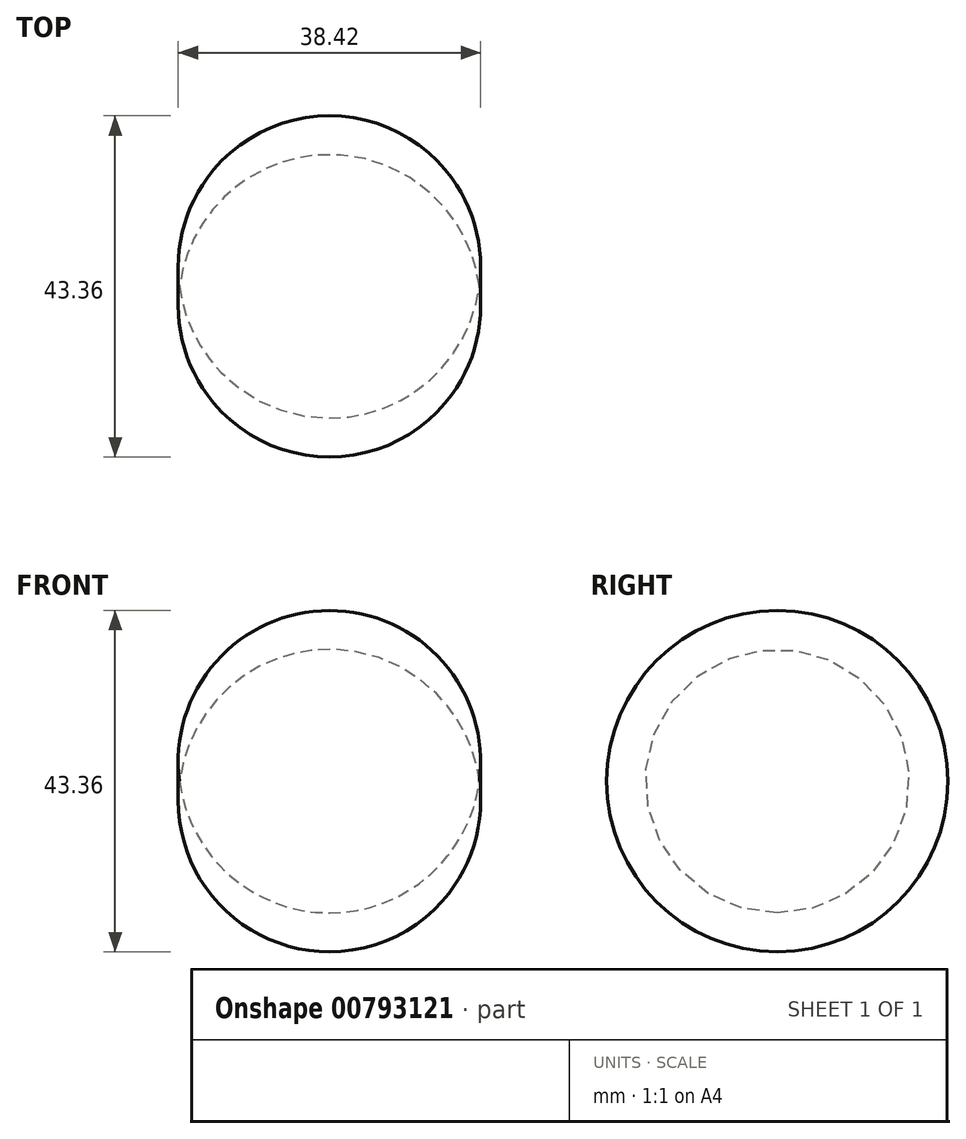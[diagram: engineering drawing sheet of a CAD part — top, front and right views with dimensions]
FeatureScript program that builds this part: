
annotation { "Feature Type Name" : "Feature", "Feature Type Description" : "" }
export const myFeature = defineFeature(function(context is Context, id is Id, definition is map)
    precondition{}
    {
        {
            var Q0;
            Q0=qCreatedBy(makeId("Front.planeOp"),FACE);
            cPlane(context, id + "F0", {"entities" : qUnion([Q0]), "cplaneType" : CPlaneType.OFFSET, "offset" : 48.26 * mm, "width" : 152.4 * mm, "height" : 152.4 * mm});
        }
        {
            var Q0;
            Q0=qCreatedBy(id+"F0.planeOp",FACE);
            var sketch = newSketch(context, id + "F1", { "sketchPlane" : qUnion([Q0])});
            skLineSegment(sketch, "E0", {"start": v(-19.05, 0) * mm, "end": v(19.05, 0) * mm});
            skArc(sketch, "E1", {"start": v(-19.05, 0) * mm, "mid": v(0, -21.68) * mm, "end": v(19.05, 0) * mm});
            skSolve(sketch);
        }
        {
            var Q0;
            Q0 = qSketchRegion(id + "F1", true);
            var Q1;
            Q1=sQuery(id+"F1.wireOp",EDGE,"E0");
            revolve(context, id + "F2", {"surfaceOperationType" : NewSurfaceOperationType.NEW, "entities" : qUnion([Q0]), "axis" : qUnion([Q1]), "revolveType" : RevolveType.FULL});
        }
    });
